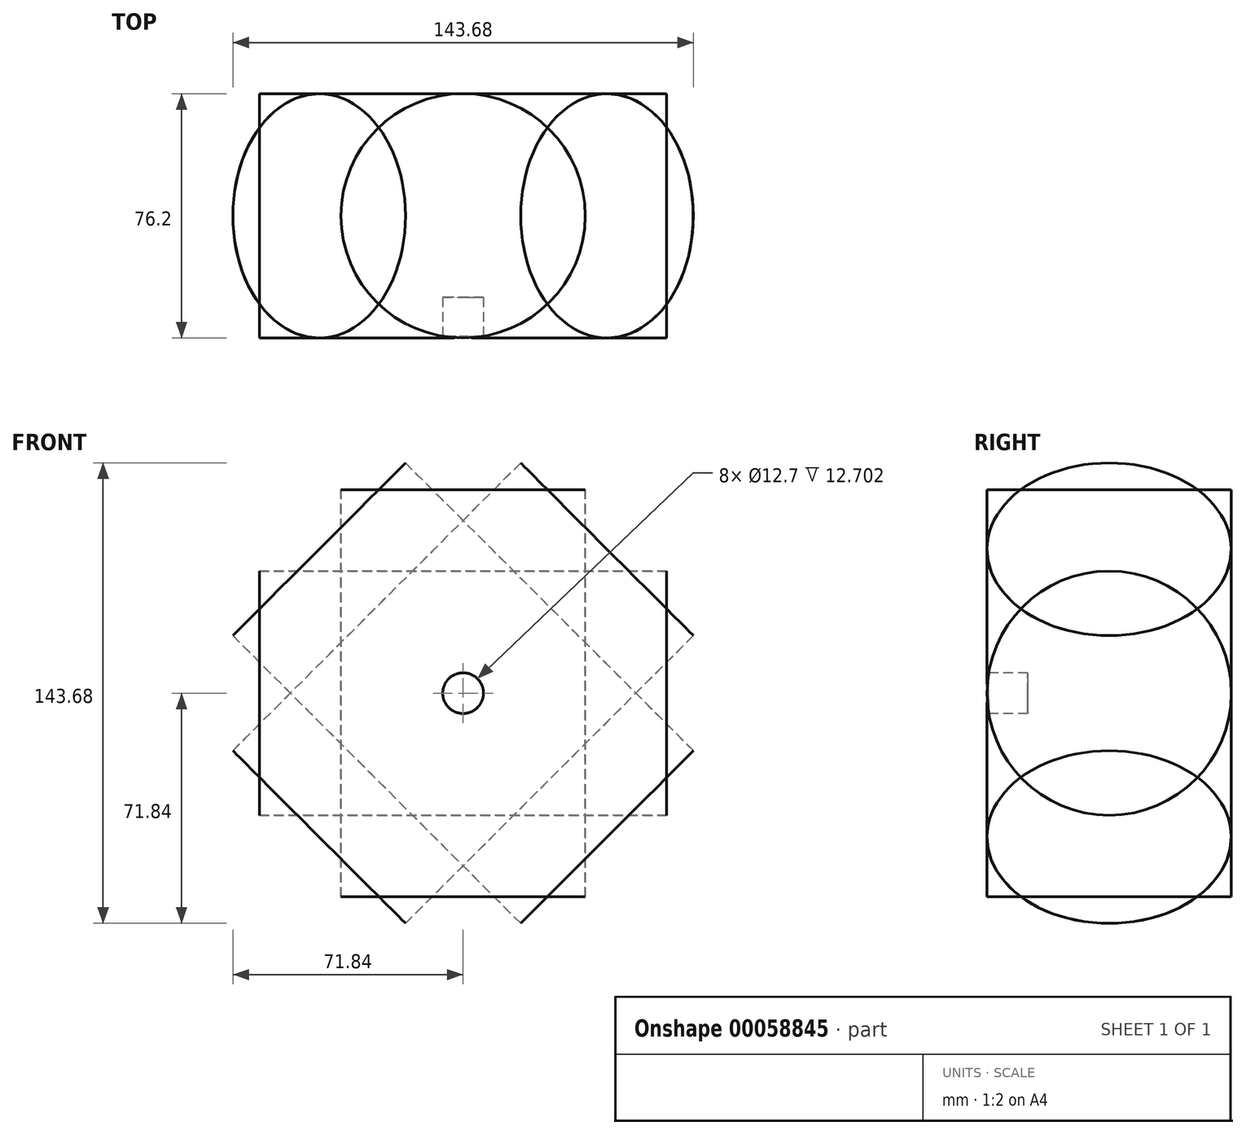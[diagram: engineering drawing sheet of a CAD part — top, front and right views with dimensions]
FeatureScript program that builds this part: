
annotation { "Feature Type Name" : "Feature", "Feature Type Description" : "" }
export const myFeature = defineFeature(function(context is Context, id is Id, definition is map)
    precondition{}
    {
        {
            var Q0;
            Q0=qCreatedBy(makeId("Front.planeOp"),FACE);
            var sketch = newSketch(context, id + "F0", { "sketchPlane" : qUnion([Q0])});
            skLineSegment(sketch, "E0.bottom", {"start": v(-38.1, 63.5) * mm, "end": v(0, 63.5) * mm});
            skLineSegment(sketch, "E0.top", {"start": v(-38.1, -63.5) * mm, "end": v(0, -63.5) * mm});
            skLineSegment(sketch, "E0.left", {"start": v(-38.1, 63.5) * mm, "end": v(-38.1, -63.5) * mm});
            skLineSegment(sketch, "E0.right", {"start": v(0, 63.5) * mm, "end": v(0, -63.5) * mm});
            skSolve(sketch);
        }
        {
            var Q0;
            Q0=makeQuery(id+"F0.imprint","IMPRINT",FACE,{"disambiguationData":[TD([[makeQuery(id+"F0.imprint","IMPRINT",EDGE,{"derivedFrom":sQuery(id+"F0.wireOp",EDGE,"E0.bottom")}),-1.0]])]});
            var Q1;
            Q1=sQuery(id+"F0.wireOp",EDGE,"E0.right");
            revolve(context, id + "F1", {"entities" : qUnion([Q0]), "axis" : qUnion([Q1]), "revolveType" : RevolveType.FULL});
        }
        {
            var Q0;
            Q0=qCreatedBy(makeId("Front.planeOp"),FACE);
            cPlane(context, id + "F2", {"entities" : qUnion([Q0]), "cplaneType" : CPlaneType.OFFSET, "offset" : 38.1 * mm, "width" : 152.4 * mm, "height" : 152.4 * mm});
        }
        {
            var Q0;
            Q0=qCreatedBy(id+"F2.planeOp",FACE);
            var sketch = newSketch(context, id + "F3", { "sketchPlane" : qUnion([Q0])});
            skCircle(sketch, "E1", {"center": v(0, 0) * mm, "radius": 6.35 * mm});
            skSolve(sketch);
        }
        {
            var Q0;
            Q0=makeQuery(id+"F3.imprint","IMPRINT",FACE,{"disambiguationData":[TD([[makeQuery(id+"F3.imprint","IMPRINT",EDGE,{"derivedFrom":sQuery(id+"F3.wireOp",EDGE,"E1")}),1.0]])]});
            extrude(context, id + "F4", {"entities" : qUnion([Q0]), "operationType" : NewBodyOperationType.REMOVE, "oppositeDirection" : true, "depth" : 12.7 * mm});
        }
        {
            var Q0;
            Q0=makeQuery(id+"F1.opRevolve","SWEPT_BODY",BODY,{"disambiguationData":[OSD([sQuery(id+"F0.wireOp",EDGE,"E0.bottom"),sQuery(id+"F0.wireOp",EDGE,"E0.top"),sQuery(id+"F0.wireOp",EDGE,"E0.left"),sQuery(id+"F0.wireOp",EDGE,"E0.right")])]});
            var Q1;
            Q1=makeQuery(id+"F4.boolean.opBoolean","COPY",EDGE,{"derivedFrom":makeQuery(id+"F4.opExtrude","CAP_EDGE",EDGE,{"disambiguationData":[OSD([sQuery(id+"F3.wireOp",EDGE,"E1")])],"isStart":false})});
            circularPattern(context, id + "F5", {"entities" : qUnion([Q0]), "axis" : qUnion([Q1]), "angle" : 360 * degree, "instanceCount" : 8, "equalSpace" : true});
        }
    });
